# Revit family: 202941001 SANITARIO MANANTIAL RD
name_source: partatom
category: Aparatos sanitarios
revit_build: Autodesk Revit 2016 (Build: 20151007_0715(x64)
units: mm (PartAtom-declared; Revit-internal decimal feet)

## family parameters
Anfitrión = Muro
Compartido = No
Corte con vacíos al cargar = No
Cota de conector redondo = Diámetro de uso
Número OmniClass = 23.45.55.00
Punto de cálculo de habitación = No
Siempre vertical = Sí
Tipo de pieza = Normal
Título OmniClass = Sanitary Faucets, Wastes

## types (1)
- Tipo 1
    Acabado = Brillante
    Alto Nominal = 700 mm  [stored 2.29659 ft]
    Ancho Nominal = 430 mm
    Característica = Alta eficiencia de agua, Cómodo perfil taza redonda, Altura tradiconal de taza para usu familiar, Válvula de descarga de fácil mantenimiento, Válvula de suministro de agua antisifón con flotador, Sofisticado botón de accionamiento de 38mm ubicado en la tapa del tanque perfectas con el asisnto y los accesorios.
    Color = Blanco
    Consumo de Agua = 4.8 LPF.
    Cumplimiento de Norma = NTC No. 920-1
    Código de montaje = D2030
    Descripción = Sanitario Manantial dos piezas descarga sencilla con botón superior
    Descripción de la garantía = Garantía Integral / 5 años garantía en grifería
    Diámetro de conexión de entrada = 12,7 mm / 1/2"
    Diámetro de conexión sanitaria = 101.6 mm / 4"
    Duración Garantía Partes = 5 años Grifería
    Duración Garantía Unidad = Años
    Fabricante = www.corona.com.co
    Forma = Rectangular
    Imagen de tipo = <Ninguno>
    Informacion del producto = https://www.corona.co
    Longitud Nominal = 670 mm  [stored 2.19816 ft]
    Material = Ceramica_Corona_Blanco
    Material Secundario = Plastico_Corona_Blanco
    Nombre = Sanitario Manantial
    Numero de Modelo = 202941001
    Presión máxima = 80 PSI
    Presión mínima = 20 PSI
    Responsable Garantia Partes = www.corona.com.co
    Tamaño = 670 x 700 x 430 mm
    Tipo de Activo = Fijo

note: [stored X ft] marks values corroborated as IEEE doubles in the binary element streams (Revit-internal decimal feet)
